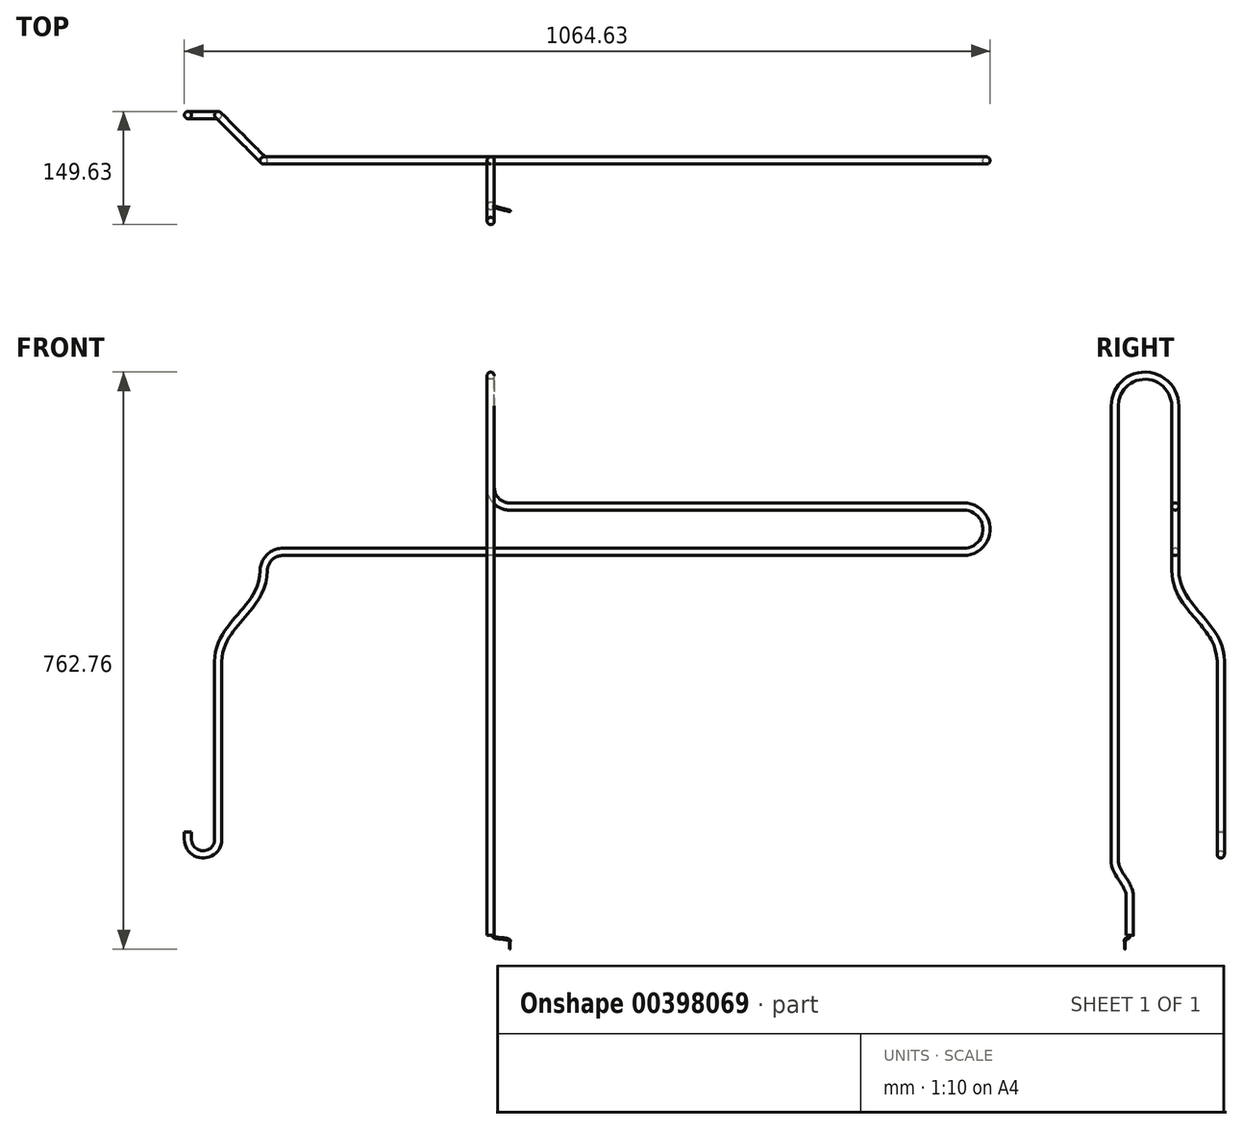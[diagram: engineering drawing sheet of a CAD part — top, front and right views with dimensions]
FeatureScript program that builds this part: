
annotation { "Feature Type Name" : "Feature", "Feature Type Description" : "" }
export const myFeature = defineFeature(function(context is Context, id is Id, definition is map)
    precondition{}
    {
        {
            var Q0;
            Q0=qCreatedBy(makeId("Top.planeOp"),FACE);
            var sketch = newSketch(context, id + "F0", { "sketchPlane" : qUnion([Q0])});
            skCircle(sketch, "E0", {"center": v(0, 0) * mm, "radius": 4.76 * mm});
            skSolve(sketch);
        }
        {
            var Q0;
            Q0=qCreatedBy(makeId("Right.planeOp"),FACE);
            var sketch = newSketch(context, id + "F1", { "sketchPlane" : qUnion([Q0])});
            skLineSegment(sketch, "E1", {"start": v(60, 592) * mm, "end": v(60, 700) * mm});
            skArc(sketch, "E2", {"start": v(60, 700) * mm, "mid": v(20, 740) * mm, "end": v(-20, 700) * mm});
            skLineSegment(sketch, "E3", {"start": v(0, 50) * mm, "end": v(0, 0) * mm});
            skFitSpline(sketch, "E4", {"points": [v(0, 50) * mm, v(-10, 75) * mm, v(-20, 100) * mm], "startDerivative": vector(0, 60) * mm, "endDerivative": vector(0, 60) * mm});
            skLineSegment(sketch, "E5", {"start": v(-20, 90) * mm, "end": v(-20, 100) * mm, "construction": true});
            skLineSegment(sketch, "E6", {"start": v(0, 60) * mm, "end": v(0, 50) * mm, "construction": true});
            skLineSegment(sketch, "E7", {"start": v(0, 50) * mm, "end": v(-20, 100) * mm, "construction": true});
            skLineSegment(sketch, "E8", {"start": v(-20, 100) * mm, "end": v(-20, 700) * mm});
            skSolve(sketch);
        }
        {
            var Q0;
            Q0=qCreatedBy(makeId("Front.planeOp"),FACE);
            var Q1;
            Q1=sQuery(id+"F1.wireOp",VERTEX,"E1.start");
            cPlane(context, id + "F2", {"entities" : qUnion([Q0, Q1]), "cplaneType" : CPlaneType.PLANE_POINT, "offset" : 25 * mm, "width" : 150 * mm, "height" : 150 * mm});
        }
        {
            var Q0;
            Q0=qCreatedBy(id+"F2.planeOp",FACE);
            var sketch = newSketch(context, id + "F3", { "sketchPlane" : qUnion([Q0])});
            skArc(sketch, "E9", {"start": v(0, 592) * mm, "mid": v(7.32, 574.32) * mm, "end": v(25, 567) * mm});
            skLineSegment(sketch, "E10", {"start": v(25, 567) * mm, "end": v(625, 567) * mm});
            skArc(sketch, "E11", {"start": v(625, 507) * mm, "mid": v(655, 537) * mm, "end": v(625, 567) * mm});
            skLineSegment(sketch, "E12", {"start": v(625, 507) * mm, "end": v(-275, 507) * mm});
            skArc(sketch, "E13", {"start": v(-275, 507) * mm, "mid": v(-292.68, 499.68) * mm, "end": v(-300, 482) * mm});
            skLineSegment(sketch, "E14", {"start": v(-300, 482) * mm, "end": v(-300, 512.14) * mm, "construction": true});
            skSolve(sketch);
        }
        {
            var Q0;
            Q0=sQuery(id+"F3.wireOp",EDGE,"E14");
            cPlane(context, id + "F4", {"entities" : qUnion([Q0]), "cplaneType" : CPlaneType.LINE_ANGLE, "offset" : 25 * mm, "angle" : 45 * degree, "width" : 150 * mm, "height" : 150 * mm});
        }
        {
            var Q0;
            Q0=qCreatedBy(id+"F4.planeOp",FACE);
            var sketch = newSketch(context, id + "F5", { "sketchPlane" : qUnion([Q0])});
            skFitSpline(sketch, "E15", {"points": [v(254.56, 482) * mm, v(297.06, 422) * mm, v(339.56, 362) * mm], "startDerivative": vector(0, -150) * mm, "endDerivative": vector(0, -150) * mm});
            skLineSegment(sketch, "E16", {"start": v(254.56, 457) * mm, "end": v(254.56, 482) * mm, "construction": true});
            skLineSegment(sketch, "E17", {"start": v(339.56, 387) * mm, "end": v(339.56, 362) * mm, "construction": true});
            skLineSegment(sketch, "E18", {"start": v(339.56, 362) * mm, "end": v(254.56, 482) * mm, "construction": true});
            skSolve(sketch);
        }
        {
            var Q0;
            Q0=qCreatedBy(makeId("Front.planeOp"),FACE);
            var Q1;
            Q1=sQuery(id+"F5.wireOp",VERTEX,"E15.2.internal");
            cPlane(context, id + "F6", {"entities" : qUnion([Q0, Q1]), "cplaneType" : CPlaneType.PLANE_POINT, "offset" : 25 * mm, "width" : 150 * mm, "height" : 150 * mm});
        }
        {
            var Q0;
            Q0=qCreatedBy(id+"F6.planeOp",FACE);
            var sketch = newSketch(context, id + "F7", { "sketchPlane" : qUnion([Q0])});
            skLineSegment(sketch, "E19", {"start": v(-360.1, 127) * mm, "end": v(-360.1, 362) * mm});
            skArc(sketch, "E20", {"start": v(-400.1, 127) * mm, "mid": v(-380.1, 107) * mm, "end": v(-360.1, 127) * mm});
            skLineSegment(sketch, "E21", {"start": v(-400.1, 127) * mm, "end": v(-400.1, 137) * mm});
            skSolve(sketch);
        }
        {
            var Q0;
            Q0=qSketchRegion(id+"F0",true);
            var Q1;
            Q1=qConstructionFilter(qBodyType(qCreatedBy(id+"F1",EDGE),BodyType.WIRE),ConstructionObject.NO);
            var Q2;
            Q2=qConstructionFilter(qBodyType(qCreatedBy(id+"F3",EDGE),BodyType.WIRE),ConstructionObject.NO);
            var Q3;
            Q3=qConstructionFilter(qBodyType(qCreatedBy(id+"F5",EDGE),BodyType.WIRE),ConstructionObject.NO);
            var Q4;
            Q4=qConstructionFilter(qBodyType(qCreatedBy(id+"F7",EDGE),BodyType.WIRE),ConstructionObject.NO);
            sweep(context, id + "F8", {"profiles" : qUnion([Q0]), "path" : qUnion([Q1, Q2, Q3, Q4])});
        }
        {
            var Q0;
            Q0=makeQuery(id+"F8.opSweep","CAP_FACE",FACE,{"disambiguationData":[OSD([sQuery(id+"F0.wireOp",EDGE,"E0"),sQuery(id+"F1.wireOp",VERTEX,"9avbEkqO-CQ4f-H5Hg-38DB-rcSkPiFHVGC0.start")])],"isStart":true});
            var sketch = newSketch(context, id + "F9", { "sketchPlane" : qUnion([Q0])});
            skCircle(sketch, "E22", {"center": v(2.9, 0.78) * mm, "radius": 1 * mm});
            skLineSegment(sketch, "E23", {"start": v(0, 0) * mm, "end": v(4.76, 0) * mm, "construction": true});
            skLineSegment(sketch, "E24", {"start": v(0, 0) * mm, "end": v(4.6, 1.23) * mm, "construction": true});
            skSolve(sketch);
        }
        {
            var Q0;
            Q0=sQuery(id+"F9.wireOp",VERTEX,"E22.center");
            var Q1;
            Q1=sQuery(id+"F9.wireOp",VERTEX,"E24.start");
            var Q2;
            Q2=sQuery(id+"F1.wireOp",VERTEX,"E3.start");
            cPlane(context, id + "F10", {"entities" : qUnion([Q0, Q1, Q2]), "cplaneType" : CPlaneType.THREE_POINT, "offset" : 25 * mm, "width" : 150 * mm, "height" : 150 * mm});
        }
        {
            var Q0;
            Q0=qCreatedBy(id+"F10.planeOp",FACE);
            var sketch = newSketch(context, id + "F11", { "sketchPlane" : qUnion([Q0])});
            skFitSpline(sketch, "E25", {"points": [v(3, 0) * mm, v(14.5, -4) * mm, v(26, -8) * mm], "startDerivative": vector(0, -18) * mm, "endDerivative": vector(0, -18) * mm});
            skLineSegment(sketch, "E26", {"start": v(3, 0) * mm, "end": v(26, -8) * mm, "construction": true});
            skLineSegment(sketch, "E27", {"start": v(26, -5) * mm, "end": v(26, -8) * mm, "construction": true});
            skLineSegment(sketch, "E28", {"start": v(3, -3) * mm, "end": v(3, 0) * mm, "construction": true});
            skSolve(sketch);
        }
        {
            var Q0;
            Q0=qSketchRegion(id+"F9",true);
            var Q1;
            Q1=qConstructionFilter(qBodyType(qCreatedBy(id+"F11",EDGE),BodyType.WIRE),ConstructionObject.NO);
            sweep(context, id + "F12", {"operationType" : NewBodyOperationType.ADD, "profiles" : qUnion([Q0]), "path" : qUnion([Q1])});
        }
        {
            var Q0;
            Q0=makeQuery(id+"F12.opSweep","CAP_FACE",FACE,{"disambiguationData":[OSD([sQuery(id+"F9.wireOp",EDGE,"E22"),sQuery(id+"F11.wireOp",VERTEX,"E25.end")])],"isStart":false});
            var sketch = newSketch(context, id + "F13", { "sketchPlane" : qUnion([Q0])});
            skCircle(sketch, "E29", {"center": v(25.11, 6.73) * mm, "radius": 0.5 * mm});
            skSolve(sketch);
        }
        {
            var Q0;
            Q0=qSketchRegion(id+"F13",true);
            extrude(context, id + "F14", {"entities" : qUnion([Q0]), "operationType" : NewBodyOperationType.ADD, "depth" : 10 * mm});
        }
    });
